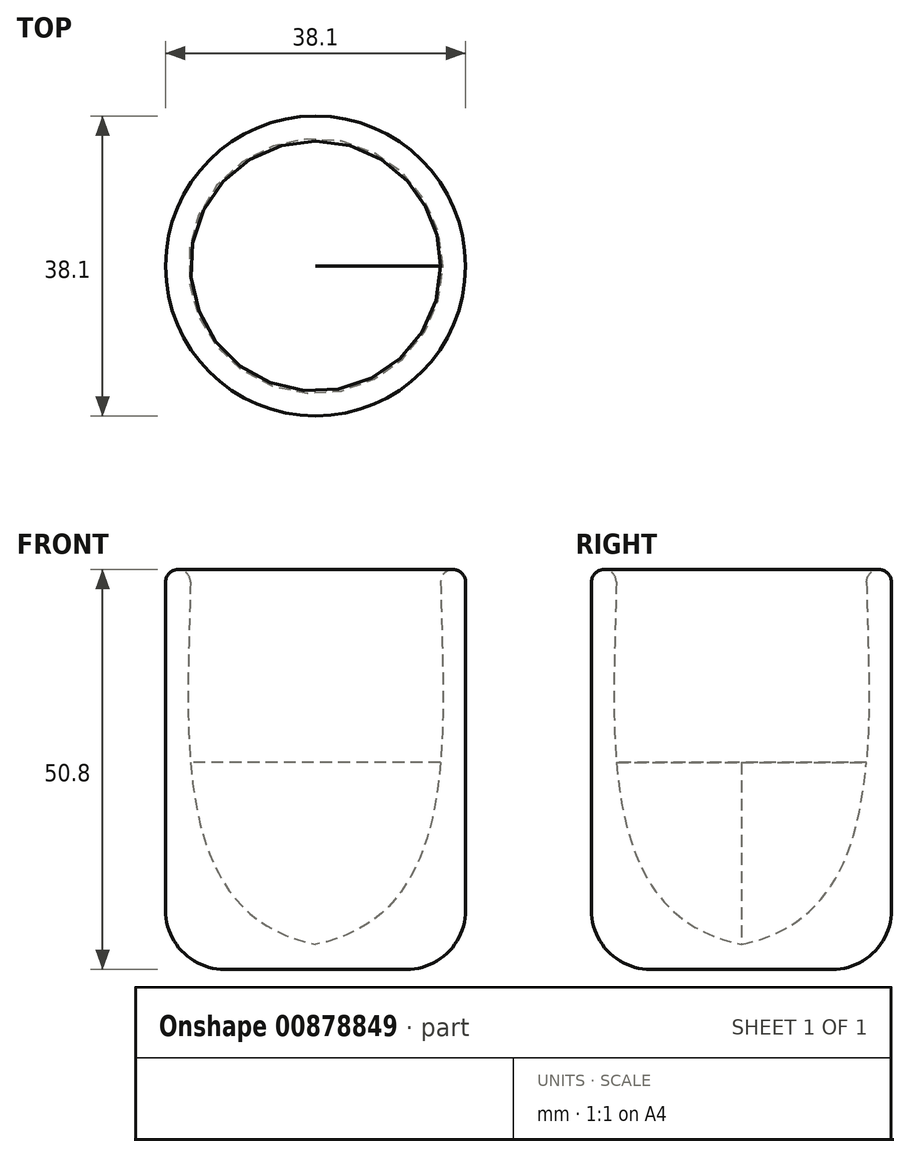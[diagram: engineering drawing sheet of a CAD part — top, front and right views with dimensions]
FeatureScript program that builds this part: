
annotation { "Feature Type Name" : "Feature", "Feature Type Description" : "" }
export const myFeature = defineFeature(function(context is Context, id is Id, definition is map)
    precondition{}
    {
        {
            var Q0;
            Q0=qCreatedBy(makeId("Front.planeOp"),FACE);
            var sketch = newSketch(context, id + "F0", { "sketchPlane" : qUnion([Q0])});
            skLineSegment(sketch, "E0.bottom", {"start": v(0, 0) * mm, "end": v(19.05, 0) * mm});
            skLineSegment(sketch, "E0.top", {"start": v(0, -50.8) * mm, "end": v(19.05, -50.8) * mm});
            skLineSegment(sketch, "E0.left", {"start": v(0, 0) * mm, "end": v(0, -50.8) * mm});
            skLineSegment(sketch, "E0.right", {"start": v(19.05, 0) * mm, "end": v(19.05, -50.8) * mm});
            skLineSegment(sketch, "E1", {"start": v(0, -47.63) * mm, "end": v(19.05, -47.63) * mm});
            skLineSegment(sketch, "E2", {"start": v(15.88, 0) * mm, "end": v(15.88, -47.63) * mm});
            skPoint(sketch, "E3.4.internal.snap0", {"position": v(9.53, 0) * mm});
            skFitSpline(sketch, "E4", {"points": [v(15.88, 0) * mm, v(0, -47.63) * mm, v(-129.01, 26.24) * mm, v(0, 39.46) * mm, v(15.88, 0) * mm]});
            skSolve(sketch);
        }
        {
            var Q0;
            {var subQ1=sQuery(id+"F0.wireOp",EDGE,"E1");var subQ3=sQuery(id+"F0.wireOp",EDGE,"E2");var subQ4=makeQuery(id+"F0.imprint","INTERSECT",VERTEX,{"derivedFrom":[subQ1,subQ3]});Q0=makeQuery(id+"F0.imprint","IMPRINT",FACE,{"disambiguationData":[TD([[makeQuery(id+"F0.imprint","IMPRINT",EDGE,{"disambiguationData":[TD([[subQ4,1.0]])],"derivedFrom":subQ3}),-1.0]])]});}
            var Q1;
            {var subQ1=sQuery(id+"F0.wireOp",EDGE,"E0.top");Q1=makeQuery(id+"F0.imprint","IMPRINT",FACE,{"disambiguationData":[TD([[makeQuery(id+"F0.imprint","IMPRINT",EDGE,{"derivedFrom":subQ1}),1.0]])]});}
            var Q2;
            {var subQ1=sQuery(id+"F0.wireOp",EDGE,"E0.right");var subQ7=sQuery(id+"F0.wireOp",EDGE,"E0.bottom");var subQ8=makeQuery(id+"F0.imprint","INTERSECT",VERTEX,{"derivedFrom":[subQ7,subQ1]});Q2=makeQuery(id+"F0.imprint","IMPRINT",FACE,{"disambiguationData":[TD([[makeQuery(id+"F0.imprint","IMPRINT",EDGE,{"disambiguationData":[TD([[subQ8,-1.0]])],"derivedFrom":subQ1}),-1.0]])]});}
            var Q3;
            Q3=sQuery(id+"F0.wireOp",EDGE,"E0.left");
            revolve(context, id + "F1", {"surfaceOperationType" : NewSurfaceOperationType.NEW, "entities" : qUnion([Q0, Q1, Q2]), "axis" : qUnion([Q3]), "revolveType" : RevolveType.FULL});
        }
        {
            var Q0;
            Q0=makeQuery(id+"F1.opRevolve","SWEPT_FACE",FACE,{"disambiguationData":[OSD([sQuery(id+"F0.wireOp",EDGE,"E0.top")])]});
            fillet(context, id + "F2", {"entities" : qUnion([Q0]), "radius" : 7.5 * mm, "tangentPropagation" : true, "allowEdgeOverflow" : false});
        }
        {
            var Q0;
            Q0=makeQuery(id+"F1.opRevolve","SWEPT_FACE",FACE,{"disambiguationData":[OSD([sQuery(id+"F0.wireOp",EDGE,"E0.bottom")])]});
            fillet(context, id + "F3", {"entities" : qUnion([Q0]), "radius" : 1.57 * mm, "tangentPropagation" : true, "allowEdgeOverflow" : false});
        }
    });
